FCSTD DOCUMENT  (FreeCAD 0.19R)
Label: Board Outline
License: All rights reserved
LicenseURL: http://en.wikipedia.org/wiki/All_rights_reserved
objects: Sketcher::SketchObject×1, PartDesign::Body×1
note: 2 computed .brp shape members not serialized (recipe doc carries the construction recipe); baked Part::Feature solids carry a one-line shape summary decoded from their .brp

FEATURE [Sketcher::SketchObject] Sketch
  FullyConstrained = false
  MapMode = 5
  Support = -> [XY_Plane]
  sketch-geometry (12):
    g0: Circle CenterX=6.97792 CenterY=21.4986 CenterZ=0 NormalX=0 NormalY=0 NormalZ=1 AngleXU=0 Radius=1.1
    g1: Circle CenterX=21.4779 CenterY=17.7386 CenterZ=0 NormalX=0 NormalY=0 NormalZ=1 AngleXU=0 Radius=1.1
    g2: LineSegment StartX=8.47792 StartY=32.8986 StartZ=0 EndX=24.0279 EndY=32.8986 EndZ=0
    g3: LineSegment StartX=24.0279 StartY=32.8986 StartZ=0 EndX=24.0279 EndY=16.2386 EndZ=0
    g4: LineSegment StartX=24.0279 StartY=16.2386 StartZ=0 EndX=13.6258 EndY=1.54859 EndZ=0
    g5: LineSegment StartX=13.6258 StartY=1.54859 StartZ=0 EndX=3.47581 EndY=1.54859 EndZ=0
    g6: LineSegment StartX=3.47581 StartY=1.54859 StartZ=0 EndX=-3.14208 EndY=12.0586 EndZ=0
    g7: LineSegment StartX=-3.14208 StartY=12.0586 StartZ=0 EndX=8.47792 EndY=32.8986 EndZ=0
    g8: LineSegment StartX=9.27792 StartY=22.7986 StartZ=0 EndX=22.5279 EndY=22.7986 EndZ=0
    g9: LineSegment StartX=22.5279 StartY=22.7986 StartZ=0 EndX=22.5279 EndY=34.5986 EndZ=0
    g10: LineSegment StartX=22.5279 StartY=34.5986 StartZ=0 EndX=9.27792 EndY=34.5986 EndZ=0
    g11: LineSegment StartX=9.27792 StartY=34.5986 StartZ=0 EndX=9.27792 EndY=22.7986 EndZ=0
  constraints (34):
    c: Horizontal(g2)
    c: Coincident(g2,g3)
    c: Vertical(g3)
    c: Coincident(g3,g4)
    c: Coincident(g4,g5)
    c: Horizontal(g5)
    c: Coincident(g5,g6)
    c: Coincident(g6,g7)
    c: Coincident(g7,g2)
    c: DistanceY(g4,g2) = 31.35
    c: DistanceX(g2,g2) = 15.55
    c: DistanceY(g3,g3) = 16.66
    c: DistanceX(g6,g2) = 27.17
    c: DistanceX(g5,g5) = 10.15
    c: Distance(g6) = 12.42
    c: Distance(g4) = 18
    c: Radius(g1) = 1.1
    c: Radius(g0) = 1.1
    c: DistanceX(g1,g3) = 2.55
    c: DistanceY(g1,g2) = 15.16
    c: DistanceX(g0,g3) = 17.05
    c: DistanceY(g5,g0) = 19.95
    c: Coincident(g8,g9)
    c: Coincident(g9,g10)
    c: Coincident(g10,g11)
    c: Coincident(g11,g8)
    c: Horizontal(g8)
    c: Horizontal(g10)
    c: Vertical(g9)
    c: Vertical(g11)
    c: DistanceX(g10,g10) = 13.25
    c: DistanceY(g9,g9) = 11.8
    c: DistanceX(g9,g2) = 1.5
    c: DistanceY(g2,g9) = 1.7
FEATURE [PartDesign::Body] Body
  Group = -> [Sketch]
  Origin = -> Origin
